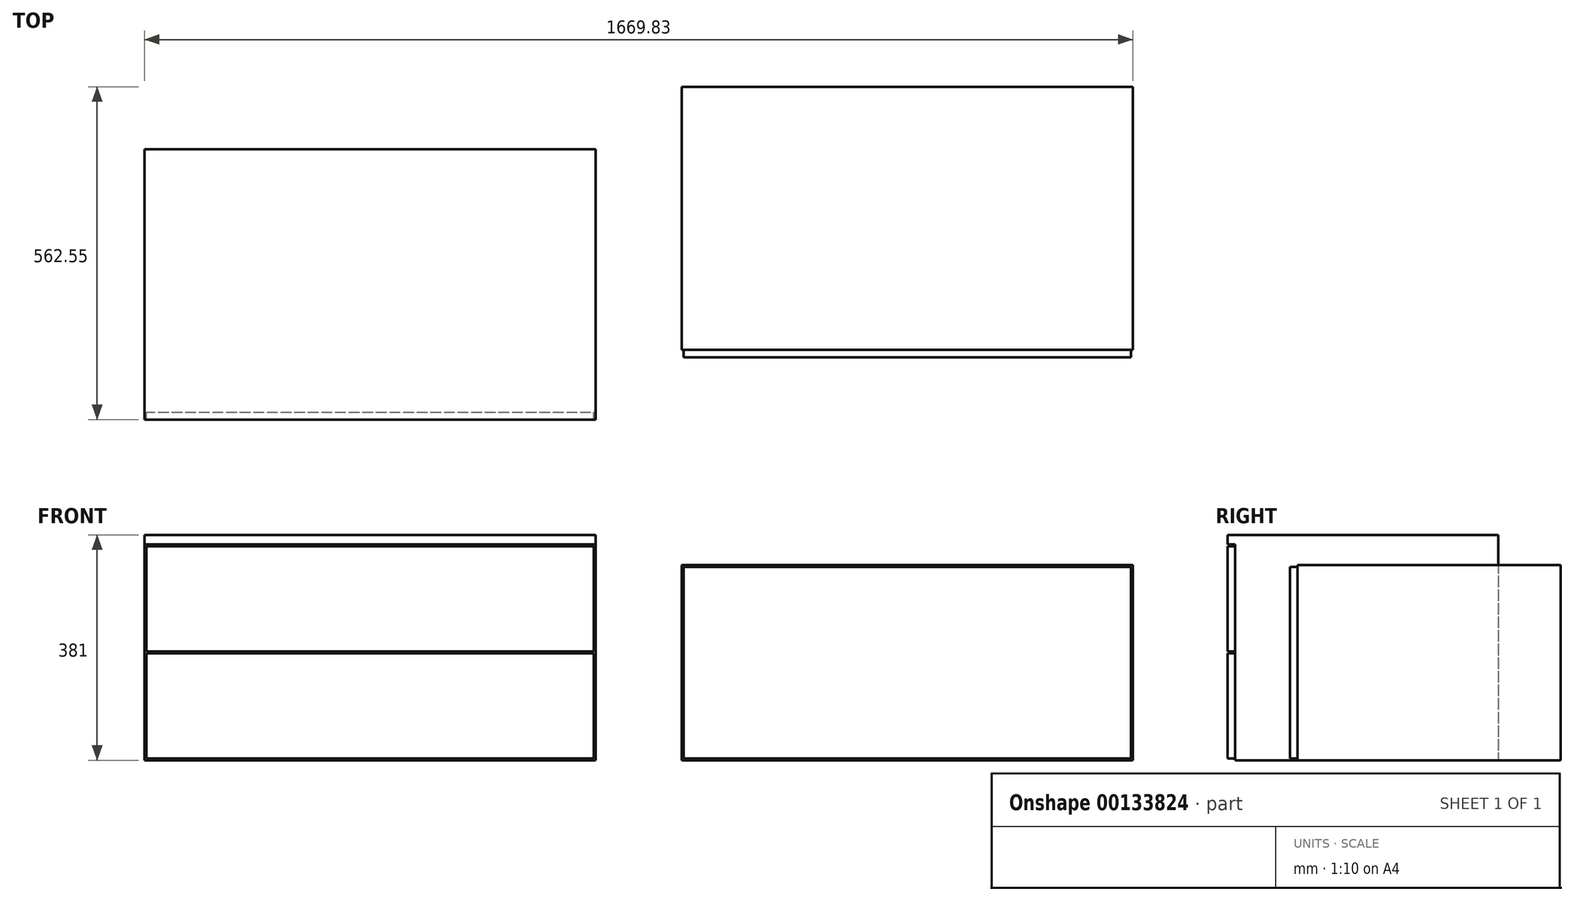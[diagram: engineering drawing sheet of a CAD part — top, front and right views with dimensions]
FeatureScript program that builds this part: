
annotation { "Feature Type Name" : "Feature", "Feature Type Description" : "" }
export const myFeature = defineFeature(function(context is Context, id is Id, definition is map)
    precondition{}
    {
        {
            var Q0;
            Q0=qCreatedBy(makeId("Top.planeOp"),FACE);
            var sketch = newSketch(context, id + "F0", { "sketchPlane" : qUnion([Q0])});
            skLineSegment(sketch, "E0.bottom", {"start": v(-659.6, 220.02) * mm, "end": v(102.4, 220.02) * mm});
            skLineSegment(sketch, "E0.top", {"start": v(-659.6, -224.48) * mm, "end": v(102.4, -224.48) * mm});
            skLineSegment(sketch, "E0.left", {"start": v(-659.6, 220.02) * mm, "end": v(-659.6, -224.48) * mm});
            skLineSegment(sketch, "E0.right", {"start": v(102.4, 220.02) * mm, "end": v(102.4, -224.48) * mm});
            skSolve(sketch);
        }
        {
            var Q0;
            Q0 = qSketchRegion(id + "F0", true);
            extrude(context, id + "F1", {"entities" : qUnion([Q0]), "depth" : 381 * mm});
        }
        {
            var Q0;
            Q0=makeQuery(id+"F1.opExtrude","SWEPT_FACE",FACE,{"disambiguationData":[OSD([sQuery(id+"F0.wireOp",EDGE,"E0.top")])]});
            var sketch = newSketch(context, id + "F2", { "sketchPlane" : qUnion([Q0])});
            skLineSegment(sketch, "E1.bottom", {"start": v(-656.42, 180.98) * mm, "end": v(99.23, 180.98) * mm});
            skLineSegment(sketch, "E1.top", {"start": v(-656.42, 3.17) * mm, "end": v(99.23, 3.17) * mm});
            skLineSegment(sketch, "E1.left", {"start": v(-656.42, 180.98) * mm, "end": v(-656.42, 3.17) * mm});
            skLineSegment(sketch, "E1.right", {"start": v(99.23, 180.98) * mm, "end": v(99.23, 3.18) * mm});
            skLineSegment(sketch, "E2.bottom", {"start": v(-656.42, 361.95) * mm, "end": v(99.23, 361.95) * mm});
            skLineSegment(sketch, "E2.top", {"start": v(-656.42, 184.15) * mm, "end": v(99.23, 184.15) * mm});
            skLineSegment(sketch, "E2.left", {"start": v(-656.42, 361.95) * mm, "end": v(-656.42, 184.15) * mm});
            skLineSegment(sketch, "E2.right", {"start": v(99.23, 361.95) * mm, "end": v(99.23, 184.15) * mm});
            skLineSegment(sketch, "E3.bottom", {"start": v(-659.6, 381) * mm, "end": v(102.4, 381) * mm});
            skLineSegment(sketch, "E3.top", {"start": v(-659.6, 365.13) * mm, "end": v(102.4, 365.13) * mm});
            skLineSegment(sketch, "E3.left", {"start": v(-659.6, 381) * mm, "end": v(-659.6, 365.13) * mm});
            skLineSegment(sketch, "E3.right", {"start": v(102.4, 381) * mm, "end": v(102.4, 365.13) * mm});
            skSolve(sketch);
        }
        {
            var Q0;
            Q0=makeQuery(id+"F2.imprint","IMPRINT",FACE,{"disambiguationData":[TD([[makeQuery(id+"F2.imprint","IMPRINT",EDGE,{"derivedFrom":sQuery(id+"F2.wireOp",EDGE,"E1.bottom")}),-1.0]])]});
            var Q1;
            Q1=makeQuery(id+"F2.imprint","IMPRINT",FACE,{"disambiguationData":[TD([[makeQuery(id+"F2.imprint","IMPRINT",EDGE,{"derivedFrom":sQuery(id+"F2.wireOp",EDGE,"E2.bottom")}),-1.0]])]});
            var Q2;
            Q2=makeQuery(id+"F2.imprint","IMPRINT",FACE,{"disambiguationData":[TD([[makeQuery(id+"F2.imprint","IMPRINT",EDGE,{"derivedFrom":sQuery(id+"F2.wireOp",EDGE,"E3.bottom")}),-1.0]])]});
            extrude(context, id + "F3", {"entities" : qUnion([Q0, Q1, Q2]), "operationType" : NewBodyOperationType.ADD, "depth" : 12.7 * mm});
        }
        {
            var Q0;
            Q0=qCreatedBy(makeId("Top.planeOp"),FACE);
            var sketch = newSketch(context, id + "F4", { "sketchPlane" : qUnion([Q0])});
            skLineSegment(sketch, "E4.bottom", {"start": v(248.23, 325.37) * mm, "end": v(1010.23, 325.37) * mm});
            skLineSegment(sketch, "E4.top", {"start": v(248.23, -119.13) * mm, "end": v(1010.23, -119.13) * mm});
            skLineSegment(sketch, "E4.left", {"start": v(248.23, 325.37) * mm, "end": v(248.23, -119.13) * mm});
            skLineSegment(sketch, "E4.right", {"start": v(1010.23, 325.37) * mm, "end": v(1010.23, -119.13) * mm});
            skSolve(sketch);
        }
        {
            var Q0;
            Q0=makeQuery(id+"F4.imprint","IMPRINT",FACE,{"disambiguationData":[TD([[makeQuery(id+"F4.imprint","IMPRINT",EDGE,{"derivedFrom":sQuery(id+"F4.wireOp",EDGE,"E4.bottom")}),-1.0]])]});
            extrude(context, id + "F5", {"entities" : qUnion([Q0]), "depth" : 330.2 * mm});
        }
        {
            var Q0;
            Q0=makeQuery(id+"F5.opExtrude","SWEPT_FACE",FACE,{"disambiguationData":[OSD([sQuery(id+"F4.wireOp",EDGE,"E4.top")])]});
            var sketch = newSketch(context, id + "F6", { "sketchPlane" : qUnion([Q0])});
            skLineSegment(sketch, "E5.bottom", {"start": v(251.4, 327.03) * mm, "end": v(1007.06, 327.03) * mm});
            skLineSegment(sketch, "E5.top", {"start": v(251.4, 3.18) * mm, "end": v(1007.06, 3.18) * mm});
            skLineSegment(sketch, "E5.left", {"start": v(251.4, 327.03) * mm, "end": v(251.4, 3.18) * mm});
            skLineSegment(sketch, "E5.right", {"start": v(1007.06, 327.03) * mm, "end": v(1007.06, 3.18) * mm});
            skSolve(sketch);
        }
        {
            var Q0;
            Q0 = qSketchRegion(id + "F6", true);
            extrude(context, id + "F7", {"entities" : qUnion([Q0]), "operationType" : NewBodyOperationType.ADD, "depth" : 12.7 * mm});
        }
    });
